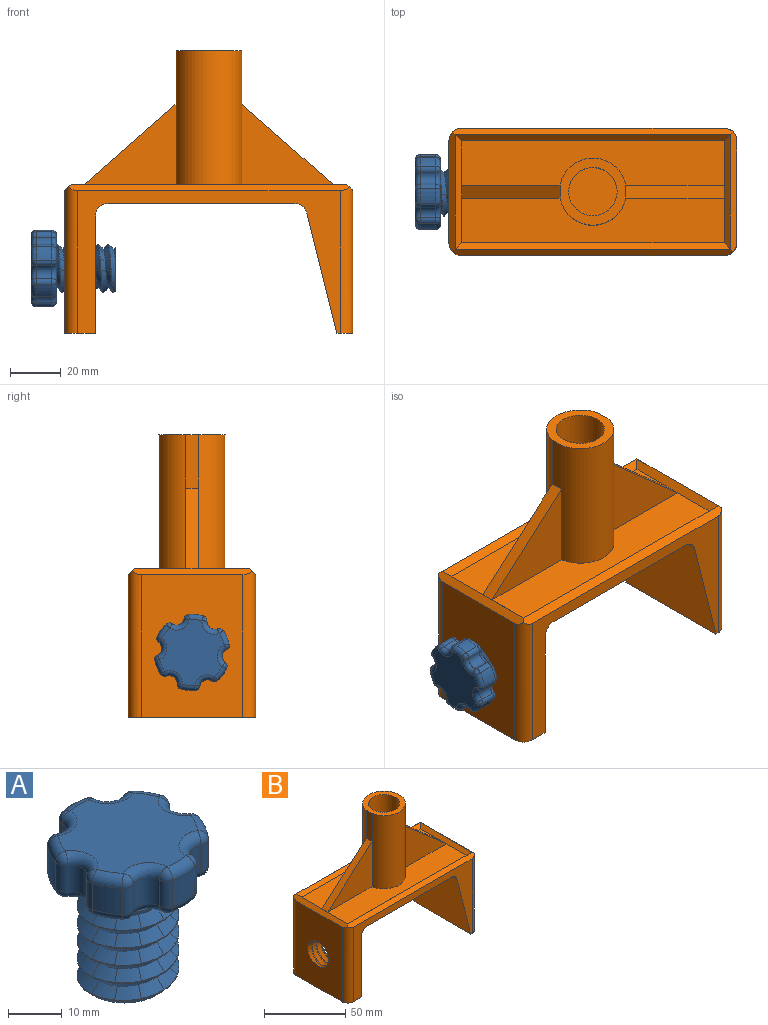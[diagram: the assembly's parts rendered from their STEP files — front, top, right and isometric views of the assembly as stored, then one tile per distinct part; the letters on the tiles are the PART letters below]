
ASSEMBLY  parts=2 mates=1
PART A: 193 faces, bbox 30.5x32.1x37.1 mm
  f0: cylinder r=9.5mm len=23mm, axis (0,0,-1), area 69mm2, adj f1,f2,f3,f4,f5,f6,f7,f8
  f1: bspline ~19.2x19mm, area 48.9mm2, adj f0,f2,f190,f191,f192
  f2: bspline ~4.43x4.43mm, area 12mm2, adj f0,f1,f3,f189
  f3: bspline ~14.25x10.97mm, area 12mm2, adj f0,f2,f4,f188
  f4: bspline ~16.45x5.7mm, area 12mm2, adj f0,f3,f5,f187
  f5: bspline ~14.25x10.97mm, area 12mm2, adj f0,f4,f6,f186
  f6: bspline ~9.5x4.39mm, area 12mm2, adj f0,f5,f7,f185
  f7: bspline ~16.45x5.71mm, area 12mm2, adj f0,f6,f8,f184
  f8: bspline ~4.43x4.43mm, area 12mm2, adj f0,f7,f9,f183
  f9: bspline ~14.25x10.97mm, area 12.1mm2, adj f0,f8,f10,f182
  f10: bspline ~8.23x5.7mm, area 12mm2, adj f0,f9,f11,f181
  f11: bspline ~14.25x10.97mm, area 12mm2, adj f0,f10,f12,f180
  f12: bspline ~4.75x2.92mm, area 12mm2, adj f0,f11,f13,f179
  f13: bspline ~16.45x5.71mm, area 12mm2, adj f0,f12,f14,f178
  f14: bspline ~14.25x10.97mm, area 12mm2, adj f0,f13,f15,f177
  f15: bspline ~14.25x10.97mm, area 12mm2, adj f0,f14,f16,f176
  f16: bspline ~16.45x5.7mm, area 12mm2, adj f0,f15,f17,f175
  f17: bspline ~14.25x10.97mm, area 12mm2, adj f0,f16,f18,f174
  f18: bspline ~4.75x2.92mm, area 12mm2, adj f0,f17,f19,f173
  f19: bspline ~16.45x5.7mm, area 12mm2, adj f0,f18,f20,f172
  f20: bspline ~4.43x4.43mm, area 12mm2, adj f0,f19,f21,f171
  f21: bspline ~14.25x10.97mm, area 12mm2, adj f0,f20,f22,f170
  f22: bspline ~8.23x5.7mm, area 12mm2, adj f0,f21,f23,f169
  f23: bspline ~14.25x10.97mm, area 12mm2, adj f0,f22,f24,f168
  f24: bspline ~9.5x4.39mm, area 12mm2, adj f0,f23,f25,f167
  f25: bspline ~16.45x5.71mm, area 12mm2, adj f0,f24,f26,f166
  f26: bspline ~14.25x10.97mm, area 12mm2, adj f0,f25,f27,f165
  f27: bspline ~14.25x10.97mm, area 12.1mm2, adj f0,f26,f28,f164
  f28: bspline ~16.45x5.7mm, area 12mm2, adj f0,f27,f29,f163
  f29: bspline ~14.25x10.97mm, area 12.1mm2, adj f0,f28,f30,f162
  f30: bspline ~9.5x4.39mm, area 12mm2, adj f0,f29,f31,f161
  f31: bspline ~16.45x5.71mm, area 12mm2, adj f0,f30,f32,f160
  f32: bspline ~4.43x4.43mm, area 12mm2, adj f0,f31,f33,f159
  f33: bspline ~14.25x10.97mm, area 12mm2, adj f0,f32,f34,f158
  f34: bspline ~16.45x5.7mm, area 12mm2, adj f0,f33,f35,f157
  f35: bspline ~14.25x10.97mm, area 12mm2, adj f0,f34,f36,f156
  f36: bspline ~4.75x2.92mm, area 12mm2, adj f0,f35,f37,f155
  f37: bspline ~16.45x5.71mm, area 12mm2, adj f0,f36,f38,f154
  f38: bspline ~14.25x10.97mm, area 12mm2, adj f0,f37,f39,f153
  f39: bspline ~14.25x10.97mm, area 12mm2, adj f0,f38,f40,f152
  f40: bspline ~16.45x5.7mm, area 12mm2, adj f0,f39,f41,f151
  f41: bspline ~14.25x10.97mm, area 12.1mm2, adj f0,f40,f42,f150
  f42: bspline ~9.5x4.39mm, area 12mm2, adj f0,f41,f43,f149
  f43: bspline ~16.45x5.7mm, area 12mm2, adj f0,f42,f44,f148
  f44: bspline ~4.43x4.43mm, area 12mm2, adj f0,f43,f45,f147
  f45: bspline ~14.25x10.97mm, area 12mm2, adj f0,f44,f46,f146
  f46: bspline ~16.45x5.7mm, area 12mm2, adj f0,f45,f47,f145
  f47: bspline ~14.25x10.97mm, area 12mm2, adj f0,f46,f48,f144
  f48: bspline ~14.25x10.97mm, area 12mm2, adj f0,f47,f49,f143
  f49: bspline ~16.45x5.71mm, area 12mm2, adj f0,f48,f50,f142
  f50: bspline ~14.25x10.97mm, area 12mm2, adj f0,f49,f51,f141
  f51: bspline ~14.25x10.97mm, area 12mm2, adj f0,f50,f52,f140
  f52: bspline ~16.45x5.7mm, area 12mm2, adj f0,f51,f53,f139
  f53: bspline ~14.25x10.97mm, area 12mm2, adj f0,f52,f54,f138
  f54: bspline ~14.25x10.97mm, area 12mm2, adj f0,f53,f55,f137
  f55: bspline ~16.45x5.71mm, area 12mm2, adj f0,f54,f56,f136
  f56: bspline ~4.43x4.43mm, area 12mm2, adj f0,f55,f57,f135
  f57: bspline ~14.25x10.97mm, area 12.1mm2, adj f0,f56,f58,f134
  f58: bspline ~21.94x19mm, area 107.7mm2, adj f0,f57,f59,f134
  f59: plane 27.53x26.13mm, normal (0,0,-1), area 192.1mm2, adj f0,f58,f60,f123,f124,f125,f126,f127
  f60: torus R=5mm, axis (0,0,1), area 23.4mm2, adj f59,f61,f120,f121,f122
  f61: cylinder r=3mm len=6mm, axis (0,0,-1), area 36mm2, adj f60,f62,f118,f119
  f62: cylinder r=2mm len=6mm, axis (0,0,1), area 16mm2, adj f61,f63,f117,f122
  f63: cylinder r=15mm len=6mm, axis (0,0,-1), area 34.9mm2, adj f62,f64,f115,f133
  f64: torus R=13mm, axis (0,0,1), area 17.4mm2, adj f63,f65,f114,f117
  f65: plane 26x24.6mm, normal (0,0,1), area 425.4mm2, adj f64,f66,f104,f105,f106,f107,f108,f109
  f66: torus R=5mm, axis (0,0,1), area 23.4mm2, adj f65,f67,f75,f103
  f67: sphere r=2mm, area 5.3mm2, adj f66,f68,f113
  f68: cylinder r=2mm len=6mm, axis (0,0,1), area 16mm2, adj f67,f69,f74,f75
  f69: cylinder r=15mm len=6mm, axis (0,0,-1), area 34.9mm2, adj f68,f70,f113,f131
  f70: cylinder r=2mm len=6mm, axis (0,0,1), area 16mm2, adj f69,f71,f72,f73
  f71: cylinder r=3mm len=6mm, axis (0,0,-1), area 36mm2, adj f70,f112,f115,f132
  f72: sphere r=2mm, area 3.4mm2, adj f70,f131,f132
  f73: sphere r=2mm, area 5.3mm2, adj f70,f112,f113
  f74: sphere r=2mm, area 7.6mm2, adj f68,f130,f131
  f75: cylinder r=3mm len=6mm, axis (0,0,-1), area 36mm2, adj f66,f68,f76,f130
  f76: cylinder r=2mm len=6mm, axis (0,0,1), area 16mm2, adj f75,f77,f78,f103
  f77: sphere r=2mm, area 7.9mm2, adj f76,f129,f130
  f78: cylinder r=15mm len=6mm, axis (0,0,-1), area 34.9mm2, adj f76,f79,f104,f129
  f79: cylinder r=2mm len=6mm, axis (0,0,1), area 16mm2, adj f78,f80,f81,f102
  f80: sphere r=2mm, area 5.3mm2, adj f79,f128,f129
  f81: cylinder r=3mm len=6mm, axis (0,0,-1), area 36mm2, adj f79,f82,f105,f128
  f82: cylinder r=2mm len=6mm, axis (0,0,1), area 16mm2, adj f81,f83,f100,f101
  f83: cylinder r=15mm len=6mm, axis (0,0,-1), area 34.9mm2, adj f82,f84,f106,f127
  f84: cylinder r=2mm len=6mm, axis (0,0,1), area 16mm2, adj f83,f85,f98,f99
  f85: cylinder r=3mm len=6mm, axis (0,0,-1), area 36mm2, adj f84,f86,f107,f126
  f86: cylinder r=2mm len=6mm, axis (0,0,1), area 16mm2, adj f85,f87,f96,f97
  f87: cylinder r=15mm len=6mm, axis (0,0,-1), area 34.9mm2, adj f86,f88,f108,f125
  f88: cylinder r=2mm len=6mm, axis (0,0,1), area 16mm2, adj f87,f89,f94,f95
  f89: cylinder r=3mm len=6mm, axis (0,0,-1), area 36mm2, adj f88,f90,f109,f124
  f90: cylinder r=2mm len=6mm, axis (0,0,1), area 16mm2, adj f89,f91,f92,f93
  f91: cylinder r=15mm len=6mm, axis (0,0,-1), area 34.9mm2, adj f90,f110,f118,f123
  f92: sphere r=2mm, area 5.7mm2, adj f90,f109,f110
  f93: sphere r=2mm, area 7.9mm2, adj f90,f123,f124
  f94: sphere r=2mm, area 9.4mm2, adj f88,f108,f109
  f95: sphere r=2mm, area 3.5mm2, adj f88,f124,f125
  f96: sphere r=2mm, area 5.3mm2, adj f86,f107,f108
  f97: sphere r=2mm, area 5.3mm2, adj f86,f125,f126
  f98: sphere r=2mm, area 7.1mm2, adj f84,f106,f107
  f99: sphere r=2mm, area 5.3mm2, adj f84,f126,f127
  f100: sphere r=2mm, area 5.3mm2, adj f82,f105,f106
  f101: sphere r=2mm, area 5.3mm2, adj f82,f127,f128
  f102: sphere r=2mm, area 5.4mm2, adj f79,f104,f105
  f103: sphere r=2mm, area 2.7mm2, adj f66,f76,f104
  f104: torus R=13mm, axis (0,0,1), area 17.4mm2, adj f65,f78,f102,f103
  f105: torus R=5mm, axis (0,0,1), area 23.4mm2, adj f65,f81,f100,f102
  f106: torus R=13mm, axis (0,0,1), area 17.4mm2, adj f65,f83,f98,f100
  f107: torus R=5mm, axis (0,0,1), area 23.4mm2, adj f65,f85,f96,f98
  f108: torus R=13mm, axis (0,0,1), area 17.4mm2, adj f65,f87,f94,f96
  f109: torus R=5mm, axis (0,0,1), area 23.4mm2, adj f65,f89,f92,f94
  f110: torus R=13mm, axis (0,0,1), area 17.4mm2, adj f65,f91,f92,f111
  f111: sphere r=2mm, area 8mm2, adj f110,f118,f119
  f112: torus R=5mm, axis (0,0,1), area 23.4mm2, adj f65,f71,f73,f114
  f113: torus R=13mm, axis (0,0,1), area 17.4mm2, adj f65,f67,f69,f73
  f114: sphere r=2mm, area 7.1mm2, adj f64,f112,f115
  f115: cylinder r=2mm len=6mm, axis (0,0,1), area 16mm2, adj f63,f71,f114,f116
  f116: sphere r=2mm, area 7.3mm2, adj f115,f132,f133
  f117: sphere r=2mm, area 6.4mm2, adj f62,f64,f119
  f118: cylinder r=2mm len=6mm, axis (0,0,1), area 16mm2, adj f61,f91,f111,f121
  f119: torus R=5mm, axis (0,0,1), area 23.4mm2, adj f61,f65,f111,f117
  f120: sphere r=2mm, area 0.5mm2, adj f60,f123
  f121: sphere r=2mm, area 2mm2, adj f60,f118,f123
  f122: sphere r=2mm, area 6.4mm2, adj f60,f62,f133
  f123: torus R=13mm, axis (0,0,1), area 17.4mm2, adj f59,f91,f93,f120,f121
  f124: torus R=5mm, axis (0,0,1), area 23.4mm2, adj f59,f89,f93,f95
  f125: torus R=13mm, axis (0,0,1), area 17.4mm2, adj f59,f87,f95,f97
  f126: torus R=5mm, axis (0,0,1), area 23.4mm2, adj f59,f85,f97,f99
  f127: torus R=13mm, axis (0,0,1), area 17.4mm2, adj f59,f83,f99,f101
  f128: torus R=5mm, axis (0,0,1), area 23.4mm2, adj f59,f80,f81,f101
  f129: torus R=13mm, axis (0,0,1), area 17.4mm2, adj f59,f77,f78,f80
  f130: torus R=5mm, axis (0,0,1), area 23.4mm2, adj f59,f74,f75,f77
  f131: torus R=13mm, axis (0,0,1), area 17.4mm2, adj f59,f69,f72,f74
  f132: torus R=5mm, axis (0,0,1), area 23.4mm2, adj f59,f71,f72,f116
  f133: torus R=13mm, axis (0,0,1), area 17.4mm2, adj f59,f63,f116,f122
  f134: bspline ~19.2x19mm, area 48.9mm2, adj f0,f57,f58,f59,f135
  f135: bspline ~4.43x4.43mm, area 12mm2, adj f0,f56,f134,f136
  f136: bspline ~4.75x2.92mm, area 12mm2, adj f0,f55,f135,f137
  f137: bspline ~8.23x5.7mm, area 12mm2, adj f0,f54,f136,f138
  f138: bspline ~4.43x4.43mm, area 12mm2, adj f0,f53,f137,f139
  f139: bspline ~14.25x10.97mm, area 12mm2, adj f0,f52,f138,f140
  f140: bspline ~16.45x5.7mm, area 12mm2, adj f0,f51,f139,f141
  f141: bspline ~4.43x4.43mm, area 12mm2, adj f0,f50,f140,f142
  f142: bspline ~4.75x2.92mm, area 12mm2, adj f0,f49,f141,f143
  f143: bspline ~16.45x5.7mm, area 12mm2, adj f0,f48,f142,f144
  f144: bspline ~4.43x4.43mm, area 12mm2, adj f0,f47,f143,f145
  f145: bspline ~14.25x10.97mm, area 12mm2, adj f0,f46,f144,f146
  f146: bspline ~4.75x2.92mm, area 12mm2, adj f0,f45,f145,f147
  f147: bspline ~4.43x4.43mm, area 12mm2, adj f0,f44,f146,f148
  f148: bspline ~4.75x2.92mm, area 12mm2, adj f0,f43,f147,f149
  f149: bspline ~4.75x2.92mm, area 12mm2, adj f0,f42,f148,f150
  f150: bspline ~14.25x10.97mm, area 12.1mm2, adj f0,f41,f149,f151
  f151: bspline ~9.5x4.39mm, area 12mm2, adj f0,f40,f150,f152
  f152: bspline ~4.75x2.92mm, area 12mm2, adj f0,f39,f151,f153
  f153: bspline ~14.25x10.97mm, area 12mm2, adj f0,f38,f152,f154
  f154: bspline ~4.75x2.92mm, area 12mm2, adj f0,f37,f153,f155
  f155: bspline ~4.75x2.92mm, area 12mm2, adj f0,f36,f154,f156
  f156: bspline ~14.25x10.97mm, area 12mm2, adj f0,f35,f155,f157
  f157: bspline ~9.5x4.39mm, area 12mm2, adj f0,f34,f156,f158
  f158: bspline ~16.45x5.7mm, area 12mm2, adj f0,f33,f157,f159
  f159: bspline ~4.43x4.43mm, area 12mm2, adj f0,f32,f158,f160
  f160: bspline ~4.75x2.92mm, area 12mm2, adj f0,f31,f159,f161
  f161: bspline ~8.23x5.7mm, area 12mm2, adj f0,f30,f160,f162
  f162: bspline ~14.25x10.97mm, area 12.1mm2, adj f0,f29,f161,f163
  f163: bspline ~4.75x2.92mm, area 12mm2, adj f0,f28,f162,f164
  f164: bspline ~16.45x5.7mm, area 12.1mm2, adj f0,f27,f163,f165
  f165: bspline ~4.43x4.43mm, area 12mm2, adj f0,f26,f164,f166
  f166: bspline ~4.75x2.92mm, area 12mm2, adj f0,f25,f165,f167
  f167: bspline ~4.75x2.92mm, area 12mm2, adj f0,f24,f166,f168
  f168: bspline ~4.43x4.43mm, area 12mm2, adj f0,f23,f167,f169
  f169: bspline ~4.75x2.92mm, area 12mm2, adj f0,f22,f168,f170
  f170: bspline ~16.45x5.7mm, area 12mm2, adj f0,f21,f169,f171
  f171: bspline ~4.43x4.43mm, area 12mm2, adj f0,f20,f170,f172
  f172: bspline ~9.5x4.39mm, area 12mm2, adj f0,f19,f171,f173
  f173: bspline ~4.75x2.92mm, area 12mm2, adj f0,f18,f172,f174
  f174: bspline ~4.43x4.43mm, area 12mm2, adj f0,f17,f173,f175
  f175: bspline ~14.25x10.97mm, area 12mm2, adj f0,f16,f174,f176
  f176: bspline ~16.45x5.7mm, area 12mm2, adj f0,f15,f175,f177
  f177: bspline ~4.43x4.43mm, area 12mm2, adj f0,f14,f176,f178
  f178: bspline ~14.25x10.97mm, area 12mm2, adj f0,f13,f177,f179
  f179: bspline ~16.45x5.7mm, area 12mm2, adj f0,f12,f178,f180
  f180: bspline ~4.43x4.43mm, area 12mm2, adj f0,f11,f179,f181
  f181: bspline ~14.25x10.97mm, area 12mm2, adj f0,f10,f180,f182
  f182: bspline ~16.45x5.7mm, area 12.1mm2, adj f0,f9,f181,f183
  f183: bspline ~4.43x4.43mm, area 12mm2, adj f0,f8,f182,f184
  f184: bspline ~14.25x10.97mm, area 12mm2, adj f0,f7,f183,f185
  f185: bspline ~16.45x5.7mm, area 12mm2, adj f0,f6,f184,f186
  f186: bspline ~14.25x10.97mm, area 12mm2, adj f0,f5,f185,f187
  f187: bspline ~14.25x10.97mm, area 12mm2, adj f0,f4,f186,f188
  f188: bspline ~16.45x5.7mm, area 12mm2, adj f0,f3,f187,f189
  f189: bspline ~4.43x4.43mm, area 12mm2, adj f0,f2,f188,f190
  f190: bspline ~14.25x10.97mm, area 12.1mm2, adj f0,f1,f189,f191
  f191: bspline ~19x18.98mm, area 107.7mm2, adj f0,f1,f190,f192
  f192: plane 18.78x18.65mm, normal (0,0,-1), area 233.2mm2, adj f0,f1,f191
PART B: 43 faces, bbox 115.6x50x111 mm
  f0: bspline ~23.09x20mm, area 114.1mm2, adj f1,f3,f34,f36
  f1: bspline ~20.21x20mm, area 38.9mm2, adj f0,f2,f34,f36
  f2: bspline ~23.09x20mm, area 420.1mm2, adj f1,f3,f30,f36
  f3: bspline ~23.09x20mm, area 345mm2, adj f0,f2,f30,f36
  f4: plane 73.1x50mm, normal (0,0,-1), area 3654.8mm2, adj f29,f31,f37,f38
  f5: plane 103x17.5mm, normal (0,0,1), area 1596.2mm2, adj f7,f12,f13,f20,f22,f27
  f6: plane 38.59x34mm, normal (0,-1,0), area 656mm2, adj f9,f11,f16
  f7: plane 38.59x34mm, normal (0,1,0), area 656mm2, adj f5,f12,f16
  f8: plane 26.3x25.82mm, normal (0,0,1), area 258.1mm2, adj f11,f12,f14,f17,f18
  f9: plane 103x17.5mm, normal (0,0,1), area 1596.2mm2, adj f6,f10,f11,f20,f21,f22
  f10: plane 38.59x34mm, normal (0,-1,0), area 656mm2, adj f9,f11,f19
  f11: cylinder r=13.15mm len=55mm, axis (0,0,-1), area 1995.5mm2, adj f6,f8,f9,f10,f17,f18
  f12: cylinder r=13.15mm len=55mm, axis (0,0,-1), area 1995.5mm2, adj f5,f7,f8,f13,f17,f18
  f13: plane 38.59x34mm, normal (0,1,0), area 656mm2, adj f5,f12,f19
  f14: cylinder r=9.5mm len=55mm, axis (0,0,-1), area 3283mm2, adj f8,f15
  f15: plane 19x19mm, normal (0,0,1), area 283.5mm2, adj f14
  f16: plane 38.59x34mm, normal (0.66,0,0.75), area 257.2mm2, adj f6,f7,f17,f20
  f17: plane 21x5mm, normal (1,0,0), area 105mm2, adj f8,f11,f12,f16
  f18: plane 21x5mm, normal (-1,0,0), area 105mm2, adj f8,f11,f12,f19
  f19: plane 38.59x34mm, normal (-0.66,0,0.75), area 257.2mm2, adj f10,f13,f18,f22
  f20: plane 45x2.5mm, normal (-0.71,0,0.71), area 150.3mm2, adj f5,f9,f16,f21,f23,f27
  f21: plane 108x2.5mm, normal (0,0.71,0.71), area 373mm2, adj f9,f20,f22,f26
  f22: plane 45x2.5mm, normal (0.71,0,0.71), area 150.3mm2, adj f5,f9,f19,f21,f25,f27
  f23: plane 47.07x2.5mm, normal (0.71,0,0.71), area 160.4mm2, adj f20,f24,f26,f28,f39,f40
  f24: plane 110.07x2.5mm, normal (0,0.71,0.71), area 383.1mm2, adj f23,f25,f27,f31,f40,f41
  f25: plane 47.07x2.5mm, normal (-0.71,0,0.71), area 160.4mm2, adj f22,f24,f26,f30,f41,f42
  f26: plane 110.07x2.5mm, normal (0,-0.71,0.71), area 383.1mm2, adj f21,f23,f25,f29,f39,f42
  f27: plane 108x2.5mm, normal (0,-0.71,0.71), area 373mm2, adj f5,f20,f22,f24
  f28: plane 56x40mm, normal (1,0,0), area 2240mm2, adj f23,f33,f39,f40
  f29: plane 103x56mm, normal (0,-1,0), area 1269.2mm2, adj f4,f26,f32,f33,f34,f35,f37,f38
  f30: plane 56x40mm, normal (-1,0,0), area 1979mm2, adj f2,f3,f25,f35,f36,f41,f42
  f31: plane 103x56mm, normal (0,1,0), area 1269.2mm2, adj f4,f24,f32,f33,f34,f35,f37,f38
  f32: plane 50x47.21mm, normal (-0.97,0,-0.24), area 2433.3mm2, adj f29,f31,f33,f37
  f33: plane 50x6.25mm, normal (0,0,-1), area 301.8mm2, adj f28,f29,f31,f32,f39,f40
  f34: plane 50x46mm, normal (1,0,0), area 2038.9mm2, adj f0,f1,f29,f31,f35,f36,f38
  f35: plane 50x12mm, normal (0,0,-1), area 589.3mm2, adj f29,f30,f31,f34,f41,f42
  f36: cylinder r=10mm len=20mm, axis (1,0,0), area 37.6mm2, adj f0,f1,f2,f3,f30,f34
  f37: cylinder r=5mm len=50mm, axis (0,-1,0), area 331.5mm2, adj f4,f29,f31,f32
  f38: cylinder r=5mm len=50mm, axis (0,1,0), area 392.7mm2, adj f4,f29,f31,f34
  f39: cylinder r=5mm len=57.46mm, axis (0,0,1), area 443.7mm2, adj f23,f26,f28,f29,f33
  f40: cylinder r=5mm len=57.46mm, axis (0,0,-1), area 443.7mm2, adj f23,f24,f28,f31,f33
  f41: cylinder r=5mm len=57.46mm, axis (0,0,1), area 443.7mm2, adj f24,f25,f30,f31,f35
  f42: cylinder r=5mm len=57.46mm, axis (0,0,-1), area 443.7mm2, adj f25,f26,f29,f30,f35
PLACE A rot(axis=(-0.2,-0.96,0.2),92.4deg) t=(-33.81,0,-25.5)mm
PLACE B t=(2.95,0,0)mm
MATE cylindrical B.f36 <-> A.f0  axis (-1,0,0) through (-53.55,0,-25.5)mm
